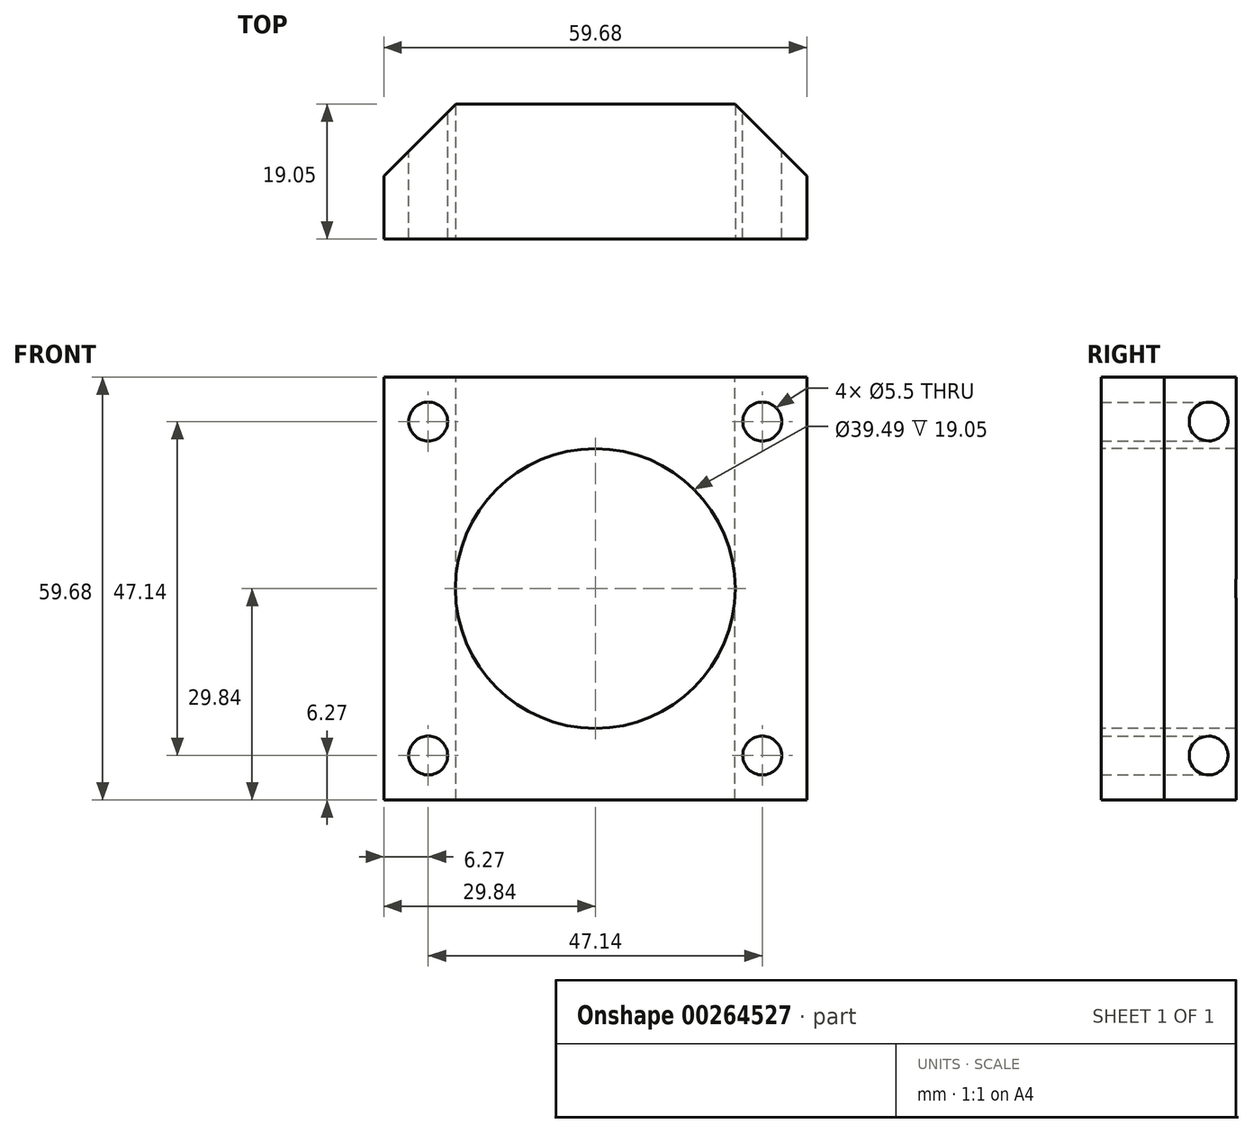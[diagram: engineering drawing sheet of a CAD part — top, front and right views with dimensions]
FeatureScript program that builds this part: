
annotation { "Feature Type Name" : "Feature", "Feature Type Description" : "" }
export const myFeature = defineFeature(function(context is Context, id is Id, definition is map)
    precondition{}
    {
        {
            var Q0;
            Q0=qCreatedBy(makeId("Front.planeOp"),FACE);
            var sketch = newSketch(context, id + "F0", { "sketchPlane" : qUnion([Q0])});
            skLineSegment(sketch, "E0.bottom", {"start": v(29.84, 29.85) * mm, "end": v(-29.84, 29.85) * mm});
            skLineSegment(sketch, "E0.top", {"start": v(29.84, -29.85) * mm, "end": v(-29.84, -29.85) * mm});
            skLineSegment(sketch, "E0.left", {"start": v(29.85, 29.84) * mm, "end": v(29.85, -29.84) * mm});
            skLineSegment(sketch, "E0.right", {"start": v(-29.84, 29.84) * mm, "end": v(-29.85, -29.84) * mm});
            skPoint(sketch, "E0.middle", {"position": v(0, 0) * mm});
            skSolve(sketch);
        }
        {
            var Q0;
            Q0 = qSketchRegion(id + "F0", true);
            extrude(context, id + "F1", {"entities" : qUnion([Q0]), "depth" : 19.05 * mm});
        }
        {
            var Q0;
            Q0=makeQuery(id+"F1.opExtrude","CAP_FACE",FACE,{"disambiguationData":[OSD([sQuery(id+"F0.wireOp",EDGE,"E0.bottom"),sQuery(id+"F0.wireOp",EDGE,"E0.top"),sQuery(id+"F0.wireOp",EDGE,"E0.left"),sQuery(id+"F0.wireOp",EDGE,"E0.right")])],"isStart":false});
            var sketch = newSketch(context, id + "F2", { "sketchPlane" : qUnion([Q0])});
            skCircle(sketch, "E1", {"center": v(0, 0) * mm, "radius": 19.74 * mm});
            skSolve(sketch);
        }
        {
            var Q0;
            Q0 = qSketchRegion(id + "F2", true);
            extrude(context, id + "F3", {"entities" : qUnion([Q0]), "operationType" : NewBodyOperationType.REMOVE, "oppositeDirection" : true, "depth" : 25.4 * mm});
        }
        {
            var Q0;
            Q0=makeQuery(id+"F1.opExtrude","CAP_FACE",FACE,{"disambiguationData":[OSD([sQuery(id+"F0.wireOp",EDGE,"E0.bottom"),sQuery(id+"F0.wireOp",EDGE,"E0.top"),sQuery(id+"F0.wireOp",EDGE,"E0.left"),sQuery(id+"F0.wireOp",EDGE,"E0.right")])],"isStart":false});
            var sketch = newSketch(context, id + "F4", { "sketchPlane" : qUnion([Q0])});
            skLineSegment(sketch, "E2.bottom", {"start": v(23.57, 23.57) * mm, "end": v(-23.57, 23.57) * mm, "construction": true});
            skLineSegment(sketch, "E2.top", {"start": v(23.57, -23.57) * mm, "end": v(-23.57, -23.57) * mm, "construction": true});
            skLineSegment(sketch, "E2.left", {"start": v(23.57, 23.57) * mm, "end": v(23.57, -23.57) * mm, "construction": true});
            skLineSegment(sketch, "E2.right", {"start": v(-23.57, 23.57) * mm, "end": v(-23.57, -23.57) * mm, "construction": true});
            skPoint(sketch, "E2.middle", {"position": v(0, 0) * mm});
            skSolve(sketch);
        }
        {
            var Q0;
            Q0=sQuery(id+"F4.wireOp",VERTEX,"E2.bottom.end");
            var Q1;
            Q1=sQuery(id+"F4.wireOp",VERTEX,"E2.left.start");
            var Q2;
            Q2=sQuery(id+"F4.wireOp",VERTEX,"E2.left.end");
            var Q3;
            Q3=sQuery(id+"F4.wireOp",VERTEX,"E2.top.end");
            var Q4;
            Q4=makeQuery(id+"F1.opExtrude","SWEPT_BODY",BODY,{"disambiguationData":[OSD([sQuery(id+"F0.wireOp",EDGE,"E0.bottom"),sQuery(id+"F0.wireOp",EDGE,"E0.top"),sQuery(id+"F0.wireOp",EDGE,"E0.left"),sQuery(id+"F0.wireOp",EDGE,"E0.right")])]});
            hole(context, id + "F5", {"style" : HoleStyle.SIMPLE, "endStyle" : HoleEndStyle.THROUGH, "standardTappedOrClearance" : lookupTablePath({ "standard" : "ISO", "fit" : "Normal", "size" : "M5", "type" : "Clearance" }), "standardBlindInLast" : lookupTablePath({ "fit" : "Standard", "standard" : "ISO", "size" : "M5", "type" : "Clearance" }), "holeDiameter" : 5.5 * mm, "tappedDepth" : 12.7 * mm, "tapClearance" : 3, "locations" : qUnion([Q0, Q1, Q2, Q3]), "scope" : qUnion([Q4]), "startStyle" : HoleStartStyle.PART});
        }
        {
            var Q0;
            Q0=makeQuery(id+"F1.opExtrude","SWEPT_FACE",FACE,{"disambiguationData":[OSD([sQuery(id+"F0.wireOp",EDGE,"E0.bottom")])]});
            var sketch = newSketch(context, id + "F6", { "sketchPlane" : qUnion([Q0])});
            skLineSegment(sketch, "E3", {"start": v(0, 0) * mm, "end": v(0, -19.05) * mm, "construction": true});
            skLineSegment(sketch, "E4", {"start": v(0, -9.53) * mm, "end": v(28.58, -9.53) * mm, "construction": true});
            skLineSegment(sketch, "E5", {"start": v(0, -9.53) * mm, "end": v(-28.57, -9.53) * mm, "construction": true});
            skPoint(sketch, "E6", {"position": v(28.58, -9.53) * mm});
            skPoint(sketch, "E7", {"position": v(-28.57, -9.53) * mm});
            skSolve(sketch);
        }
        {
            var Q0;
            {var subQ0=sQuery(id+"F0.wireOp",EDGE,"E0.bottom");Q0=makeQuery(id+"F6.imprint","IMPRINT",FACE,{"disambiguationData":[TD([[makeQuery(id+"F6.imprint","IMPRINT",EDGE,{"derivedFrom":makeQuery(id+"F1.opExtrude","CAP_EDGE",EDGE,{"disambiguationData":[OSD([subQ0])],"isStart":true})}),1.0]])]});}
            var sketch = newSketch(context, id + "F7", { "sketchPlane" : qUnion([Q0])});
            skLineSegment(sketch, "E8", {"start": v(-29.84, -10.16) * mm, "end": v(-19.68, 0) * mm});
            skLineSegment(sketch, "E9", {"start": v(-19.68, 0) * mm, "end": v(-29.84, 0) * mm});
            skLineSegment(sketch, "E10", {"start": v(-29.84, 0) * mm, "end": v(-29.84, -10.16) * mm});
            skLineSegment(sketch, "E11", {"start": v(0, 0) * mm, "end": v(0, -19.2) * mm, "construction": true});
            skLineSegment(sketch, "E12.MirrorCS", {"start": v(29.84, -10.16) * mm, "end": v(19.68, 0) * mm});
            skLineSegment(sketch, "E13.MirrorCS", {"start": v(19.68, 0) * mm, "end": v(29.84, 0) * mm});
            skLineSegment(sketch, "E14.MirrorCS", {"start": v(29.84, 0) * mm, "end": v(29.84, -10.16) * mm});
            skSolve(sketch);
        }
        {
            var Q0;
            Q0 = qSketchRegion(id + "F7", true);
            extrude(context, id + "F8", {"entities" : qUnion([Q0]), "operationType" : NewBodyOperationType.REMOVE, "endBound" : BoundingType.THROUGH_ALL, "oppositeDirection" : true, "depth" : 25.4 * mm});
        }
    });
